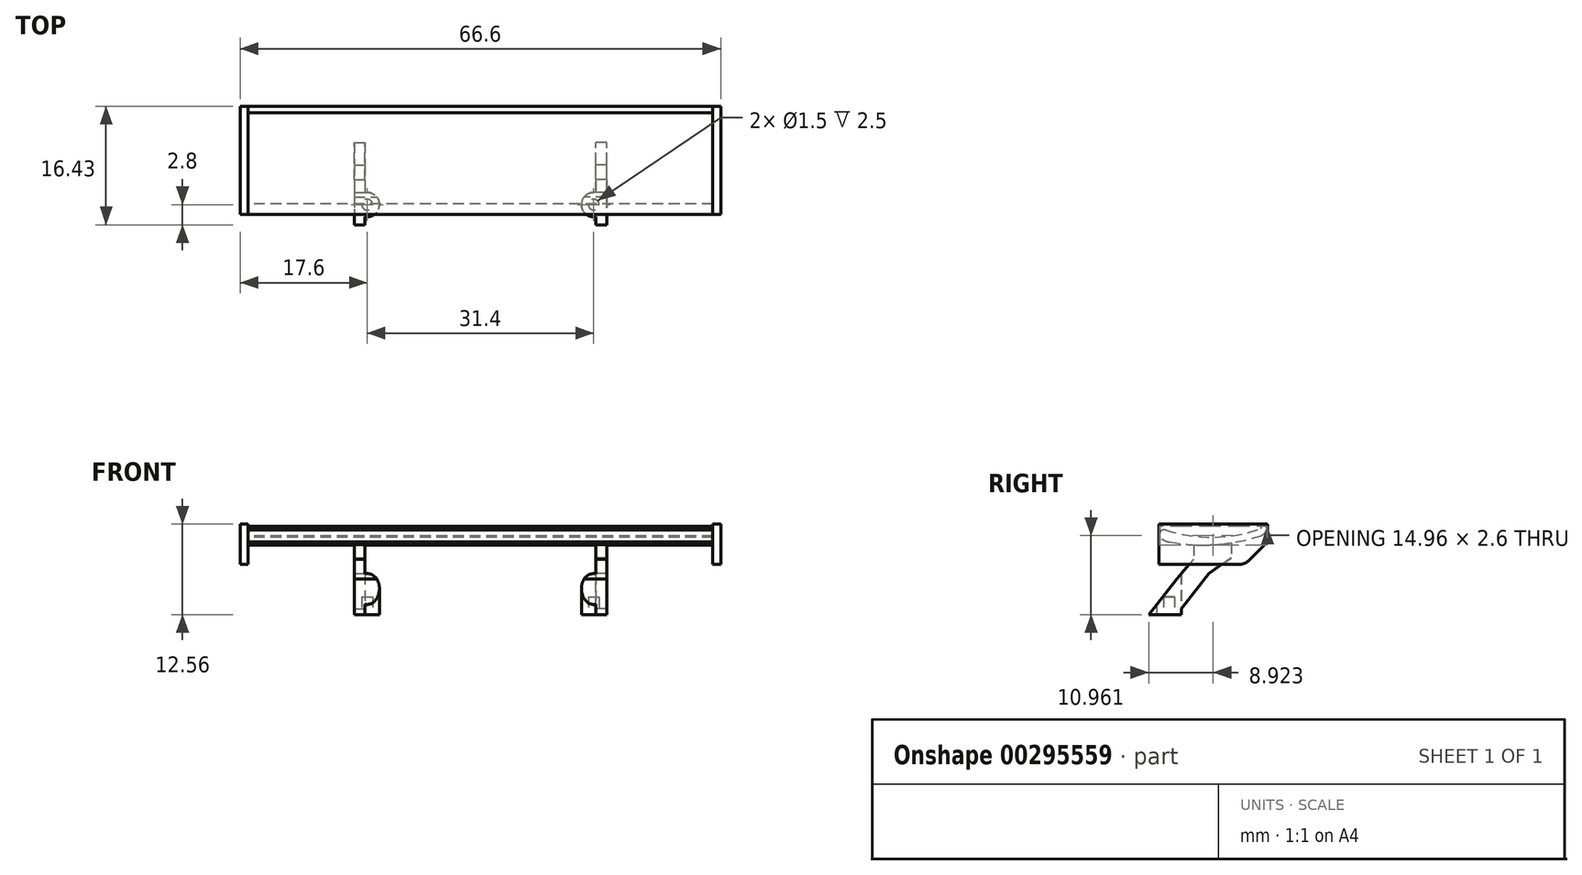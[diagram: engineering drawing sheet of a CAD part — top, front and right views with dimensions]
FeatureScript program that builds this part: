
annotation { "Feature Type Name" : "Feature", "Feature Type Description" : "" }
export const myFeature = defineFeature(function(context is Context, id is Id, definition is map)
    precondition{}
    {
        {
            var Q0;
            Q0=qCreatedBy(makeId("Right.planeOp"),FACE);
            cPlane(context, id + "F0", {"entities" : qUnion([Q0]), "cplaneType" : CPlaneType.OFFSET, "offset" : 16 * mm, "width" : 150 * mm, "height" : 150 * mm});
        }
        {
            var Q0;
            Q0=qCreatedBy(makeId("Right.planeOp"),FACE);
            cPlane(context, id + "F1", {"entities" : qUnion([Q0]), "cplaneType" : CPlaneType.OFFSET, "offset" : 16 * mm, "oppositeDirection" : true, "width" : 150 * mm, "height" : 150 * mm});
        }
        {
            var Q0;
            Q0=qCreatedBy(makeId("Right.planeOp"),FACE);
            cPlane(context, id + "F2", {"entities" : qUnion([Q0]), "cplaneType" : CPlaneType.OFFSET, "offset" : 33.3 * mm, "width" : 150 * mm, "height" : 150 * mm});
        }
        {
            var Q0;
            Q0=qCreatedBy(makeId("Right.planeOp"),FACE);
            cPlane(context, id + "F3", {"entities" : qUnion([Q0]), "cplaneType" : CPlaneType.OFFSET, "offset" : 33.3 * mm, "oppositeDirection" : true, "width" : 150 * mm, "height" : 150 * mm});
        }
        {
            var Q0;
            Q0=qCreatedBy(id+"F2.planeOp",FACE);
            var sketch = newSketch(context, id + "F4", { "sketchPlane" : qUnion([Q0])});
            skLineSegment(sketch, "E0.bottom", {"start": v(0, 0) * mm, "end": v(15, 0) * mm});
            skLineSegment(sketch, "E0.top", {"start": v(0, 5.6) * mm, "end": v(15, 5.6) * mm});
            skLineSegment(sketch, "E0.left", {"start": v(0, 0) * mm, "end": v(0, 5.6) * mm});
            skLineSegment(sketch, "E0.right", {"start": v(15, 0) * mm, "end": v(15, 5.6) * mm});
            skSolve(sketch);
        }
        {
            var Q0;
            Q0=makeQuery(id+"F4.imprint","IMPRINT",FACE,{"disambiguationData":[TD([[makeQuery(id+"F4.imprint","IMPRINT",EDGE,{"derivedFrom":sQuery(id+"F4.wireOp",EDGE,"E0.bottom")}),1.0]])]});
            extrude(context, id + "F5", {"entities" : qUnion([Q0]), "oppositeDirection" : true, "depth" : 1.1 * mm});
        }
        {
            var Q0;
            Q0=makeQuery(id+"F5.opExtrude","SWEPT_EDGE",EDGE,{"disambiguationData":[OSD([sQuery(id+"F4.wireOp",EDGE,"E0.bottom"),sQuery(id+"F4.wireOp",EDGE,"E0.right")])]});
            chamfer(context, id + "F6", {"entities" : qUnion([Q0]), "width" : 3.1 * mm, "tangentPropagation" : true});
        }
        {
            var Q0;
            Q0=qCreatedBy(id+"F3.planeOp",FACE);
            var sketch = newSketch(context, id + "F7", { "sketchPlane" : qUnion([Q0])});
            skLineSegment(sketch, "E1.bottom", {"start": v(0, 0) * mm, "end": v(15, 0) * mm});
            skLineSegment(sketch, "E1.top", {"start": v(0, 5.6) * mm, "end": v(15, 5.6) * mm});
            skLineSegment(sketch, "E1.left", {"start": v(0, 0) * mm, "end": v(0, 5.6) * mm});
            skLineSegment(sketch, "E1.right", {"start": v(15, 0) * mm, "end": v(15, 5.6) * mm});
            skSolve(sketch);
        }
        {
            var Q0;
            Q0=makeQuery(id+"F7.imprint","IMPRINT",FACE,{"disambiguationData":[TD([[makeQuery(id+"F7.imprint","IMPRINT",EDGE,{"derivedFrom":sQuery(id+"F7.wireOp",EDGE,"E1.bottom")}),1.0]])]});
            extrude(context, id + "F8", {"entities" : qUnion([Q0]), "operationType" : NewBodyOperationType.ADD, "depth" : 1.1 * mm});
        }
        {
            var Q0;
            Q0=makeQuery(id+"F8.opExtrude","SWEPT_EDGE",EDGE,{"disambiguationData":[OSD([sQuery(id+"F7.wireOp",EDGE,"E1.bottom"),sQuery(id+"F7.wireOp",EDGE,"E1.right")])]});
            chamfer(context, id + "F9", {"entities" : qUnion([Q0]), "width" : 3.1 * mm, "tangentPropagation" : true});
        }
        {
            var Q0;
            Q0=qCreatedBy(makeId("Right.planeOp"),FACE);
            var sketch = newSketch(context, id + "F10", { "sketchPlane" : qUnion([Q0])});
            skArc(sketch, "E2", {"start": v(0.92, 4.78) * mm, "mid": v(7.52, 3.79) * mm, "end": v(14.1, 4.98) * mm});
            skPoint(sketch, "E3.visualSharp", {"position": v(0, 5.1) * mm});
            skPoint(sketch, "E4.visualSharp", {"position": v(15, 4.23) * mm});
            skArc(sketch, "E4.filletArc", {"start": v(14.06, 3.98) * mm, "mid": v(14.74, 4.49) * mm, "end": v(15, 5.3) * mm});
            skLineSegment(sketch, "E5", {"start": v(15, 5.3) * mm, "end": v(14.1, 5.3) * mm});
            skLineSegment(sketch, "E6", {"start": v(14.1, 5.3) * mm, "end": v(14.1, 4.98) * mm});
            skArc(sketch, "E7", {"start": v(0.92, 4.78) * mm, "mid": v(0.08, 4.41) * mm, "end": v(0.34, 3.54) * mm});
            skArc(sketch, "E8", {"start": v(0.34, 3.54) * mm, "mid": v(0.88, 3.27) * mm, "end": v(1.46, 3.12) * mm});
            skArc(sketch, "E9", {"start": v(1.46, 3.12) * mm, "mid": v(7.81, 2.76) * mm, "end": v(14.06, 3.98) * mm});
            skPoint(sketch, "E10.start.orphan", {"position": v(15, 5.33) * mm});
            skSolve(sketch);
        }
        {
            var Q0;
            Q0=makeQuery(id+"F10.imprint","IMPRINT",FACE,{"disambiguationData":[TD([[makeQuery(id+"F10.imprint","IMPRINT",EDGE,{"derivedFrom":sQuery(id+"F10.wireOp",EDGE,"E2")}),-1.0]])]});
            extrude(context, id + "F11", {"entities" : qUnion([Q0]), "operationType" : NewBodyOperationType.ADD, "endBound" : BoundingType.SYMMETRIC, "depth" : 64.4 * mm});
        }
        {
            var Q0;
            Q0=makeQuery(id+"F11.opExtrude","SWEPT_EDGE",EDGE,{"disambiguationData":[OSD([sQuery(id+"F10.wireOp",EDGE,"E5"),sQuery(id+"F10.wireOp",EDGE,"E6")])]});
            var Q1;
            Q1=makeQuery(id+"F11.opExtrude","SWEPT_EDGE",EDGE,{"disambiguationData":[OSD([sQuery(id+"F10.wireOp",EDGE,"yVsz5IoF-Bzvb-jUyx-GidC-dmTNU0PbB6j3"),sQuery(id+"F10.wireOp",EDGE,"E5")])]});
            fillet(context, id + "F12", {"entities" : qUnion([Q0, Q1]), "radius" : 0.25 * mm, "tangentPropagation" : true, "allowEdgeOverflow" : false});
        }
        {
            var Q0;
            {var subQ0=sQuery(id+"F4.wireOp",EDGE,"E0.bottom");Q0=makeQuery(id+"F6.opChamfer","BLEND_EDGE",EDGE,{"blendedFrom":[makeQuery(id+"F5.opExtrude","SWEPT_EDGE",EDGE,{"disambiguationData":[OSD([subQ0,sQuery(id+"F4.wireOp",EDGE,"E0.right")])]}),makeQuery(id+"F5.opExtrude","SWEPT_FACE",FACE,{"disambiguationData":[OSD([subQ0])]})],"blendedInto":[makeQuery(id+"F5.opExtrude","SWEPT_FACE",FACE,{"disambiguationData":[OSD([subQ0])]})]});}
            var Q1;
            {var subQ0=sQuery(id+"F4.wireOp",EDGE,"E0.right");Q1=makeQuery(id+"F6.opChamfer","BLEND_EDGE",EDGE,{"blendedFrom":[makeQuery(id+"F5.opExtrude","SWEPT_EDGE",EDGE,{"disambiguationData":[OSD([sQuery(id+"F4.wireOp",EDGE,"E0.bottom"),subQ0])]}),makeQuery(id+"F5.opExtrude","SWEPT_FACE",FACE,{"disambiguationData":[OSD([subQ0])]})],"blendedInto":[makeQuery(id+"F5.opExtrude","SWEPT_FACE",FACE,{"disambiguationData":[OSD([subQ0])]})]});}
            var Q2;
            {var subQ0=sQuery(id+"F7.wireOp",EDGE,"E1.right");Q2=makeQuery(id+"F9.opChamfer","BLEND_EDGE",EDGE,{"blendedFrom":[makeQuery(id+"F8.opExtrude","SWEPT_EDGE",EDGE,{"disambiguationData":[OSD([sQuery(id+"F7.wireOp",EDGE,"E1.bottom"),subQ0])]}),makeQuery(id+"F8.opExtrude","SWEPT_FACE",FACE,{"disambiguationData":[OSD([subQ0])]})],"blendedInto":[makeQuery(id+"F8.opExtrude","SWEPT_FACE",FACE,{"disambiguationData":[OSD([subQ0])]})]});}
            var Q3;
            {var subQ0=sQuery(id+"F7.wireOp",EDGE,"E1.bottom");Q3=makeQuery(id+"F9.opChamfer","BLEND_EDGE",EDGE,{"blendedFrom":[makeQuery(id+"F8.opExtrude","SWEPT_EDGE",EDGE,{"disambiguationData":[OSD([subQ0,sQuery(id+"F7.wireOp",EDGE,"E1.right")])]}),makeQuery(id+"F8.opExtrude","SWEPT_FACE",FACE,{"disambiguationData":[OSD([subQ0])]})],"blendedInto":[makeQuery(id+"F8.opExtrude","SWEPT_FACE",FACE,{"disambiguationData":[OSD([subQ0])]})]});}
            fillet(context, id + "F13", {"entities" : qUnion([Q0, Q1, Q2, Q3]), "radius" : 2 * mm, "tangentPropagation" : true, "allowEdgeOverflow" : false});
        }
        {
            var Q0;
            Q0=qCreatedBy(id+"F1.planeOp",FACE);
            var sketch = newSketch(context, id + "F14", { "sketchPlane" : qUnion([Q0])});
            skLineSegment(sketch, "E11", {"start": v(4.8, 2.73) * mm, "end": v(4.8, 0.73) * mm});
            skLineSegment(sketch, "E12", {"start": v(10, 3) * mm, "end": v(10, 0.9) * mm});
            skArc(sketch, "E13", {"start": v(4.8, 2.73) * mm, "mid": v(7.4, 2.74) * mm, "end": v(10, 3) * mm});
            skLineSegment(sketch, "E14", {"start": v(3.07, -6.16) * mm, "end": v(3.07, -6.96) * mm});
            skLineSegment(sketch, "E15", {"start": v(3.07, -6.96) * mm, "end": v(-1.43, -6.96) * mm});
            skPoint(sketch, "E16.endSnap0", {"position": v(0.82, -6.96) * mm});
            skLineSegment(sketch, "E17", {"start": v(10, 0.9) * mm, "end": v(6.89, -1.28) * mm});
            skLineSegment(sketch, "E18", {"start": v(6.89, -1.28) * mm, "end": v(3.07, -6.16) * mm});
            skLineSegment(sketch, "E19", {"start": v(4.8, 0.73) * mm, "end": v(2.44, -1.98) * mm});
            skLineSegment(sketch, "E20", {"start": v(2.44, -1.98) * mm, "end": v(-1.43, -6.96) * mm});
            skSolve(sketch);
        }
        {
            var Q0;
            Q0=makeQuery(id+"F14.imprint","IMPRINT",FACE,{"disambiguationData":[TD([[makeQuery(id+"F14.imprint","IMPRINT",EDGE,{"derivedFrom":sQuery(id+"F14.wireOp",EDGE,"E11")}),1.0]])]});
            extrude(context, id + "F15", {"entities" : qUnion([Q0]), "operationType" : NewBodyOperationType.ADD, "oppositeDirection" : true, "depth" : 1.5 * mm});
        }
        {
            var Q0;
            Q0=qCreatedBy(id+"F0.planeOp",FACE);
            var sketch = newSketch(context, id + "F16", { "sketchPlane" : qUnion([Q0])});
            skLineSegment(sketch, "E21", {"start": v(-1.43, -6.96) * mm, "end": v(3.07, -6.96) * mm});
            skLineSegment(sketch, "E22", {"start": v(3.07, -6.96) * mm, "end": v(3.07, -6.16) * mm});
            skLineSegment(sketch, "E23", {"start": v(3.07, -6.16) * mm, "end": v(6.89, -1.28) * mm});
            skLineSegment(sketch, "E24", {"start": v(6.89, -1.28) * mm, "end": v(10, 0.9) * mm});
            skLineSegment(sketch, "E25", {"start": v(10, 0.9) * mm, "end": v(10, 3) * mm});
            skLineSegment(sketch, "E26", {"start": v(4.8, 0.73) * mm, "end": v(4.8, 2.73) * mm});
            skLineSegment(sketch, "E27", {"start": v(4.8, 0.73) * mm, "end": v(2.44, -1.98) * mm});
            skLineSegment(sketch, "E28", {"start": v(2.44, -1.98) * mm, "end": v(-1.43, -6.96) * mm});
            skArc(sketch, "E29", {"start": v(4.8, 2.73) * mm, "mid": v(7.4, 2.74) * mm, "end": v(10, 3) * mm});
            skSolve(sketch);
        }
        {
            var Q0;
            Q0 = qSketchRegion(id + "F16", true);
            extrude(context, id + "F17", {"entities" : qUnion([Q0]), "operationType" : NewBodyOperationType.ADD, "depth" : 1.5 * mm});
        }
        {
            var Q0;
            Q0=makeQuery(id+"F15.opExtrude","SWEPT_FACE",FACE,{"disambiguationData":[OSD([sQuery(id+"F14.wireOp",EDGE,"E15")])]});
            var sketch = newSketch(context, id + "F18", { "sketchPlane" : qUnion([Q0])});
            skLineSegment(sketch, "E30", {"start": v(18.45, -1.37) * mm, "end": v(-19.07, -1.37) * mm, "construction": true});
            skCircle(sketch, "E31", {"center": v(15.7, -1.37) * mm, "radius": 1.7 * mm});
            skCircle(sketch, "E32", {"center": v(-15.7, -1.37) * mm, "radius": 1.7 * mm});
            skSolve(sketch);
        }
        {
            var Q0;
            {var subQ0=sQuery(id+"F18.wireOp",EDGE,"E32");var subQ1=makeQuery(id+"F15.opExtrude","CAP_EDGE",EDGE,{"disambiguationData":[OSD([sQuery(id+"F14.wireOp",EDGE,"E15")])],"isStart":true});var subQ2=makeQuery(id+"F18.imprint","INTERSECT",VERTEX,{"disambiguationData":[OD(0.0)],"derivedFrom":[subQ1,subQ0]});Q0=makeQuery(id+"F18.imprint","IMPRINT",FACE,{"disambiguationData":[TD([[makeQuery(id+"F18.imprint","IMPRINT",EDGE,{"disambiguationData":[TD([[subQ2,1.0]])],"derivedFrom":subQ0}),1.0]])]});}
            var Q1;
            {var subQ0=sQuery(id+"F18.wireOp",EDGE,"E32");var subQ1=makeQuery(id+"F15.opExtrude","CAP_EDGE",EDGE,{"disambiguationData":[OSD([sQuery(id+"F14.wireOp",EDGE,"E15")])],"isStart":true});var subQ2=makeQuery(id+"F18.imprint","INTERSECT",VERTEX,{"disambiguationData":[OD(0.0)],"derivedFrom":[subQ1,subQ0]});Q1=makeQuery(id+"F18.imprint","IMPRINT",FACE,{"disambiguationData":[TD([[makeQuery(id+"F18.imprint","IMPRINT",EDGE,{"disambiguationData":[TD([[subQ2,-1.0]])],"derivedFrom":subQ0}),1.0]])]});}
            var Q2;
            Q2=makeQuery(id+"F18.imprint","IMPRINT",FACE,{"disambiguationData":[TD([[makeQuery(id+"F18.imprint","IMPRINT",EDGE,{"derivedFrom":sQuery(id+"F18.wireOp",EDGE,"E31")}),1.0]])]});
            extrude(context, id + "F19", {"entities" : qUnion([Q0, Q1, Q2]), "operationType" : NewBodyOperationType.ADD, "oppositeDirection" : true, "depth" : 6.8 * mm});
        }
        {
            var Q0;
            Q0=makeQuery(id+"F15.opExtrude","CAP_FACE",FACE,{"disambiguationData":[OSD([sQuery(id+"F14.wireOp",EDGE,"E11"),sQuery(id+"F14.wireOp",EDGE,"E12"),sQuery(id+"F14.wireOp",EDGE,"E13"),sQuery(id+"F14.wireOp",EDGE,"E14"),sQuery(id+"F14.wireOp",EDGE,"E15"),sQuery(id+"F14.wireOp",EDGE,"E17"),sQuery(id+"F14.wireOp",EDGE,"E18"),sQuery(id+"F14.wireOp",EDGE,"E19"),sQuery(id+"F14.wireOp",EDGE,"E20")])],"isStart":false});
            var sketch = newSketch(context, id + "F20", { "sketchPlane" : qUnion([Q0])});
            skLineSegment(sketch, "E33", {"start": v(1.43, -6.96) * mm, "end": v(-2.44, -1.98) * mm});
            skLineSegment(sketch, "E34", {"start": v(-2.44, -1.98) * mm, "end": v(-3.75, -0.47) * mm});
            skSolve(sketch);
        }
        {
            var Q0;
            Q0=makeQuery(id+"F15.opExtrude","SWEPT_EDGE",EDGE,{"disambiguationData":[OSD([sQuery(id+"F14.wireOp",EDGE,"E15"),sQuery(id+"F14.wireOp",EDGE,"E20")])]});
            cPlane(context, id + "F21", {"entities" : qUnion([Q0]), "cplaneType" : CPlaneType.LINE_ANGLE, "offset" : 25 * mm, "angle" : 52.14 * degree, "width" : 150 * mm, "height" : 150 * mm});
        }
        {
            var Q0;
            Q0=qCreatedBy(id+"F21.planeOp",FACE);
            var sketch = newSketch(context, id + "F22", { "sketchPlane" : qUnion([Q0])});
            skLineSegment(sketch, "E35.bottom", {"start": v(-18, 3.14) * mm, "end": v(18, 3.14) * mm});
            skLineSegment(sketch, "E35.top", {"start": v(-18, -0.86) * mm, "end": v(18, -0.86) * mm});
            skLineSegment(sketch, "E35.left", {"start": v(-18, 3.14) * mm, "end": v(-18, -0.86) * mm});
            skLineSegment(sketch, "E35.right", {"start": v(18, 3.14) * mm, "end": v(18, -0.86) * mm});
            skSolve(sketch);
        }
        {
            var Q0;
            Q0 = qSketchRegion(id + "F22", true);
            var Q1;
            Q1=sQuery(id+"F20.wireOp",EDGE,"E34");
            var Q2;
            Q2=sQuery(id+"F20.wireOp",EDGE,"E33");
            sweep(context, id + "F23", {"operationType" : NewBodyOperationType.REMOVE, "profiles" : qUnion([Q0]), "path" : qUnion([Q1, Q2])});
        }
        {
            var Q0;
            Q0=makeQuery(id+"F19.boolean.opBoolean","MERGE",FACE,{"derivedFrom":[makeQuery(id+"F15.opExtrude","SWEPT_FACE",FACE,{"disambiguationData":[OSD([sQuery(id+"F14.wireOp",EDGE,"E15")])]}),makeQuery(id+"F19.opExtrude","CAP_FACE",FACE,{"disambiguationData":[OSD([sQuery(id+"F18.wireOp",EDGE,"E32")])],"isStart":true})]});
            var sketch = newSketch(context, id + "F24", { "sketchPlane" : qUnion([Q0])});
            skCircle(sketch, "E36", {"center": v(-15.7, -1.37) * mm, "radius": 0.75 * mm});
            skCircle(sketch, "E37", {"center": v(15.7, -1.37) * mm, "radius": 0.75 * mm});
            skSolve(sketch);
        }
        {
            var Q0;
            Q0=makeQuery(id+"F24.imprint","IMPRINT",FACE,{"disambiguationData":[TD([[makeQuery(id+"F24.imprint","IMPRINT",EDGE,{"derivedFrom":sQuery(id+"F24.wireOp",EDGE,"E36")}),1.0]])]});
            var Q1;
            Q1=makeQuery(id+"F24.imprint","IMPRINT",FACE,{"disambiguationData":[TD([[makeQuery(id+"F24.imprint","IMPRINT",EDGE,{"derivedFrom":sQuery(id+"F24.wireOp",EDGE,"E37")}),1.0]])]});
            extrude(context, id + "F25", {"entities" : qUnion([Q0, Q1]), "operationType" : NewBodyOperationType.REMOVE, "oppositeDirection" : true, "depth" : 2.5 * mm});
        }
    });
